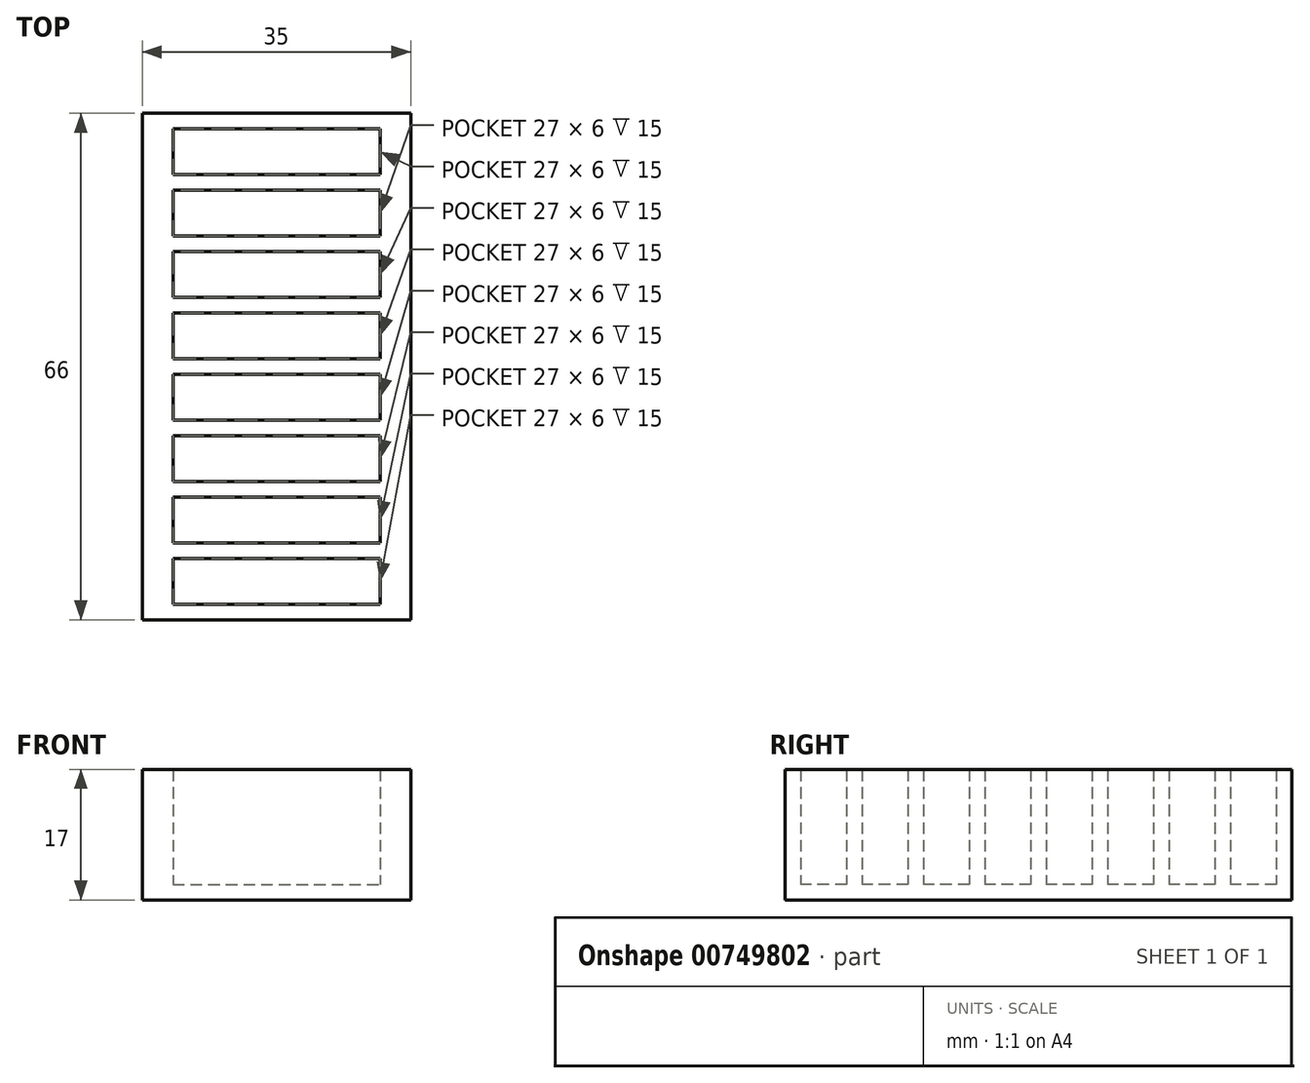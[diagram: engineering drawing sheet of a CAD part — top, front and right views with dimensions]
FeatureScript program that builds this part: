
annotation { "Feature Type Name" : "Feature", "Feature Type Description" : "" }
export const myFeature = defineFeature(function(context is Context, id is Id, definition is map)
    precondition{}
    {
        {
            var Q0;
            Q0=qCreatedBy(makeId("Top.planeOp"),FACE);
            var sketch = newSketch(context, id + "F0", { "sketchPlane" : qUnion([Q0])});
            skLineSegment(sketch, "E0.bottom", {"start": v(17.5, 33) * mm, "end": v(-17.5, 33) * mm});
            skLineSegment(sketch, "E0.top", {"start": v(17.5, -33) * mm, "end": v(-17.5, -33) * mm});
            skLineSegment(sketch, "E0.left", {"start": v(17.5, 33) * mm, "end": v(17.5, -33) * mm});
            skLineSegment(sketch, "E0.right", {"start": v(-17.5, 33) * mm, "end": v(-17.5, -33) * mm});
            skPoint(sketch, "E0.middle", {"position": v(0, 0) * mm});
            skLineSegment(sketch, "E1.bottom", {"start": v(-13.5, 31) * mm, "end": v(13.5, 31) * mm});
            skLineSegment(sketch, "E1.top", {"start": v(-13.5, 25) * mm, "end": v(13.5, 25) * mm});
            skLineSegment(sketch, "E1.left", {"start": v(-13.5, 31) * mm, "end": v(-13.5, 25) * mm});
            skLineSegment(sketch, "E1.right", {"start": v(13.5, 31) * mm, "end": v(13.5, 25) * mm});
            skLineSegment(sketch, "E2", {"start": v(-13.5, 13.1) * mm, "end": v(-17.5, 13.1) * mm, "construction": true});
            skLineSegment(sketch, "E3", {"start": v(13.5, 12.8) * mm, "end": v(17.5, 12.8) * mm, "construction": true});
            skLineSegment(sketch, "E4.bottom", {"start": v(-13.5, 23) * mm, "end": v(13.5, 23) * mm});
            skLineSegment(sketch, "E4.top", {"start": v(-13.5, 15) * mm, "end": v(13.5, 15) * mm});
            skLineSegment(sketch, "E4.left", {"start": v(-13.5, 23) * mm, "end": v(-13.5, 17) * mm});
            skLineSegment(sketch, "E4.right", {"start": v(13.5, 23) * mm, "end": v(13.5, 17) * mm});
            skLineSegment(sketch, "E5", {"start": v(-7.62, 23) * mm, "end": v(-7.62, 25) * mm, "construction": true});
            skLineSegment(sketch, "E6.bottom", {"start": v(-13.5, 17) * mm, "end": v(13.5, 17) * mm});
            skLineSegment(sketch, "E6.top", {"start": v(-13.5, 9) * mm, "end": v(13.5, 9) * mm});
            skLineSegment(sketch, "E6.left", {"start": v(-13.5, 15) * mm, "end": v(-13.5, 9) * mm});
            skLineSegment(sketch, "E6.right", {"start": v(13.5, 15) * mm, "end": v(13.5, 9) * mm});
            skLineSegment(sketch, "E7", {"start": v(-8, 17) * mm, "end": v(-8, 15) * mm, "construction": true});
            skLineSegment(sketch, "E8", {"start": v(-10.3, 31) * mm, "end": v(-10.3, 33) * mm, "construction": true});
            skLineSegment(sketch, "E9.bottom", {"start": v(-13.5, 7) * mm, "end": v(13.5, 7) * mm});
            skLineSegment(sketch, "E9.top", {"start": v(-13.5, 1) * mm, "end": v(13.5, 1) * mm});
            skLineSegment(sketch, "E9.left", {"start": v(-13.5, 7) * mm, "end": v(-13.5, 1) * mm});
            skLineSegment(sketch, "E9.right", {"start": v(13.5, 7) * mm, "end": v(13.5, 1) * mm});
            skLineSegment(sketch, "E10", {"start": v(-9.6, 7) * mm, "end": v(-9.6, 9) * mm, "construction": true});
            skLineSegment(sketch, "E11.bottom", {"start": v(-13.5, -1) * mm, "end": v(13.5, -1) * mm});
            skLineSegment(sketch, "E11.top", {"start": v(-13.5, -7) * mm, "end": v(13.5, -7) * mm});
            skLineSegment(sketch, "E11.left", {"start": v(-13.5, -1) * mm, "end": v(-13.5, -7) * mm});
            skLineSegment(sketch, "E11.right", {"start": v(13.5, -1) * mm, "end": v(13.5, -7) * mm});
            skLineSegment(sketch, "E12.bottom", {"start": v(-13.5, -9) * mm, "end": v(13.5, -9) * mm});
            skLineSegment(sketch, "E12.top", {"start": v(-13.5, -15) * mm, "end": v(13.5, -15) * mm});
            skLineSegment(sketch, "E12.left", {"start": v(-13.5, -9) * mm, "end": v(-13.5, -15) * mm});
            skLineSegment(sketch, "E12.right", {"start": v(13.5, -9) * mm, "end": v(13.5, -15) * mm});
            skLineSegment(sketch, "E13", {"start": v(-10.67, 1) * mm, "end": v(-10.67, -1) * mm, "construction": true});
            skLineSegment(sketch, "E14", {"start": v(-9.3, -9) * mm, "end": v(-9.3, -7) * mm, "construction": true});
            skLineSegment(sketch, "E15.bottom", {"start": v(-13.5, -17) * mm, "end": v(13.5, -17) * mm});
            skLineSegment(sketch, "E15.top", {"start": v(-13.5, -23) * mm, "end": v(13.5, -23) * mm});
            skLineSegment(sketch, "E15.left", {"start": v(-13.5, -17) * mm, "end": v(-13.5, -23) * mm});
            skLineSegment(sketch, "E15.right", {"start": v(13.5, -17) * mm, "end": v(13.5, -23) * mm});
            skLineSegment(sketch, "E16", {"start": v(-10.73, -15) * mm, "end": v(-10.73, -17) * mm, "construction": true});
            skLineSegment(sketch, "E17.bottom", {"start": v(-13.5, -25) * mm, "end": v(13.5, -25) * mm});
            skLineSegment(sketch, "E17.top", {"start": v(-13.5, -31) * mm, "end": v(13.5, -31) * mm});
            skLineSegment(sketch, "E17.left", {"start": v(-13.5, -25) * mm, "end": v(-13.5, -31) * mm});
            skLineSegment(sketch, "E17.right", {"start": v(13.5, -25) * mm, "end": v(13.5, -31) * mm});
            skLineSegment(sketch, "E18", {"start": v(-11.84, -25) * mm, "end": v(-11.84, -23) * mm, "construction": true});
            skSolve(sketch);
        }
        {
            var Q0;
            Q0=makeQuery(id+"F0.imprint","IMPRINT",FACE,{"disambiguationData":[TD([[makeQuery(id+"F0.imprint","IMPRINT",EDGE,{"derivedFrom":sQuery(id+"F0.wireOp",EDGE,"E0.bottom")}),1.0]])]});
            extrude(context, id + "F1", {"entities" : qUnion([Q0]), "depth" : 15 * mm, "offsetDistance" : 25 * mm});
        }
        {
            var Q0;
            Q0=makeQuery(id+"F0.imprint","IMPRINT",FACE,{"disambiguationData":[TD([[makeQuery(id+"F0.imprint","IMPRINT",EDGE,{"derivedFrom":sQuery(id+"F0.wireOp",EDGE,"E1.bottom")}),-1.0]])]});
            var Q1;
            Q1=makeQuery(id+"F0.imprint","IMPRINT",FACE,{"disambiguationData":[TD([[makeQuery(id+"F0.imprint","IMPRINT",EDGE,{"derivedFrom":sQuery(id+"F0.wireOp",EDGE,"E4.bottom")}),-1.0]])]});
            var Q2;
            Q2=makeQuery(id+"F0.imprint","IMPRINT",FACE,{"disambiguationData":[TD([[makeQuery(id+"F0.imprint","IMPRINT",EDGE,{"derivedFrom":sQuery(id+"F0.wireOp",EDGE,"E4.top")}),-1.0]])]});
            var Q3;
            Q3=makeQuery(id+"F0.imprint","IMPRINT",FACE,{"disambiguationData":[TD([[makeQuery(id+"F0.imprint","IMPRINT",EDGE,{"derivedFrom":sQuery(id+"F0.wireOp",EDGE,"E9.bottom")}),-1.0]])]});
            var Q4;
            Q4=makeQuery(id+"F0.imprint","IMPRINT",FACE,{"disambiguationData":[TD([[makeQuery(id+"F0.imprint","IMPRINT",EDGE,{"derivedFrom":sQuery(id+"F0.wireOp",EDGE,"E11.bottom")}),-1.0]])]});
            var Q5;
            Q5=makeQuery(id+"F0.imprint","IMPRINT",FACE,{"disambiguationData":[TD([[makeQuery(id+"F0.imprint","IMPRINT",EDGE,{"derivedFrom":sQuery(id+"F0.wireOp",EDGE,"E12.bottom")}),-1.0]])]});
            var Q6;
            Q6=makeQuery(id+"F0.imprint","IMPRINT",FACE,{"disambiguationData":[TD([[makeQuery(id+"F0.imprint","IMPRINT",EDGE,{"derivedFrom":sQuery(id+"F0.wireOp",EDGE,"E15.bottom")}),-1.0]])]});
            var Q7;
            Q7=makeQuery(id+"F0.imprint","IMPRINT",FACE,{"disambiguationData":[TD([[makeQuery(id+"F0.imprint","IMPRINT",EDGE,{"derivedFrom":sQuery(id+"F0.wireOp",EDGE,"E17.bottom")}),-1.0]])]});
            var Q8;
            Q8=makeQuery(id+"F0.imprint","IMPRINT",FACE,{"disambiguationData":[TD([[makeQuery(id+"F0.imprint","IMPRINT",EDGE,{"derivedFrom":sQuery(id+"F0.wireOp",EDGE,"E0.bottom")}),1.0]])]});
            extrude(context, id + "F2", {"entities" : qUnion([Q0, Q1, Q2, Q3, Q4, Q5, Q6, Q7, Q8]), "operationType" : NewBodyOperationType.ADD, "oppositeDirection" : true, "depth" : 2 * mm, "offsetDistance" : 25 * mm});
        }
    });
